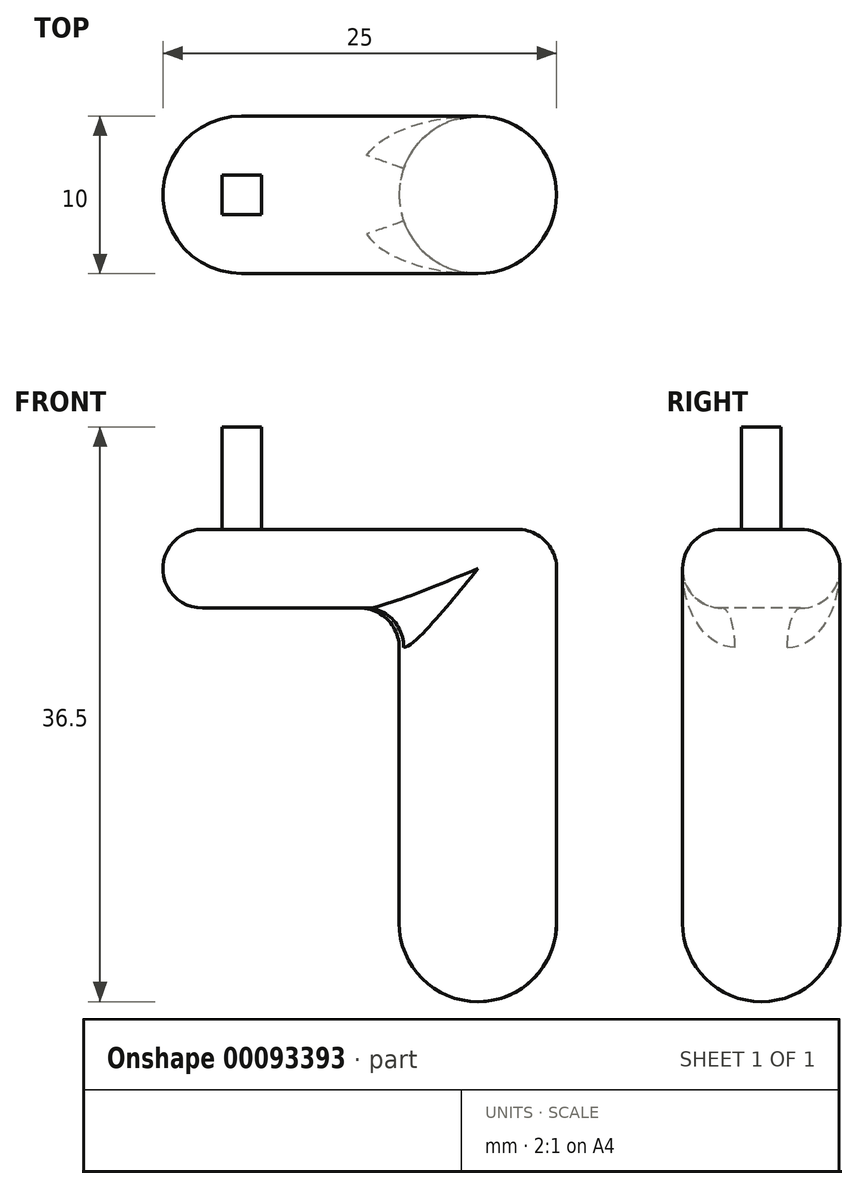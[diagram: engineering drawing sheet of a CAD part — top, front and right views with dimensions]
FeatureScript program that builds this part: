
annotation { "Feature Type Name" : "Feature", "Feature Type Description" : "" }
export const myFeature = defineFeature(function(context is Context, id is Id, definition is map)
    precondition{}
    {
        {
            var Q0;
            Q0=qCreatedBy(makeId("Top.planeOp"),FACE);
            var sketch = newSketch(context, id + "F0", { "sketchPlane" : qUnion([Q0])});
            skLineSegment(sketch, "E0.bottom", {"start": v(0, 0) * mm, "end": v(15, 0) * mm});
            skLineSegment(sketch, "E0.top", {"start": v(0, 10) * mm, "end": v(15, 10) * mm});
            skLineSegment(sketch, "E0.left", {"start": v(0, 0) * mm, "end": v(0, 10) * mm});
            skLineSegment(sketch, "E0.right", {"start": v(15, 0) * mm, "end": v(15, 10) * mm});
            skArc(sketch, "E1", {"start": v(0, 10) * mm, "mid": v(-5, 5) * mm, "end": v(0, 0) * mm});
            skArc(sketch, "E2", {"start": v(15, 0) * mm, "mid": v(20, 5) * mm, "end": v(15, 10) * mm});
            skArc(sketch, "E3", {"start": v(15, 10) * mm, "mid": v(10, 5) * mm, "end": v(15, 0) * mm});
            skLineSegment(sketch, "E4.bottom", {"start": v(1.25, 6.25) * mm, "end": v(-1.25, 6.25) * mm});
            skLineSegment(sketch, "E4.top", {"start": v(1.25, 3.75) * mm, "end": v(-1.25, 3.75) * mm});
            skLineSegment(sketch, "E4.left", {"start": v(1.25, 6.25) * mm, "end": v(1.25, 3.75) * mm});
            skLineSegment(sketch, "E4.right", {"start": v(-1.25, 6.25) * mm, "end": v(-1.25, 3.75) * mm});
            skSolve(sketch);
        }
        {
            var Q0;
            {var subQ5=sQuery(id+"F0.wireOp",EDGE,"E0.bottom");Q0=makeQuery(id+"F0.imprint","IMPRINT",FACE,{"disambiguationData":[TD([[makeQuery(id+"F0.imprint","IMPRINT",EDGE,{"derivedFrom":subQ5}),1.0]])]});}
            var Q1;
            {var subQ4=sQuery(id+"F0.wireOp",EDGE,"E1");Q1=makeQuery(id+"F0.imprint","IMPRINT",FACE,{"disambiguationData":[TD([[makeQuery(id+"F0.imprint","IMPRINT",EDGE,{"derivedFrom":subQ4}),1.0]])]});}
            extrude(context, id + "F1", {"entities" : qUnion([Q0, Q1]), "depth" : 5 * mm});
        }
        {
            var Q0;
            {var subQ5=sQuery(id+"F0.wireOp",EDGE,"E4.right");Q0=makeQuery(id+"F0.imprint","IMPRINT",FACE,{"disambiguationData":[TD([[makeQuery(id+"F0.imprint","IMPRINT",EDGE,{"derivedFrom":subQ5}),1.0]])]});}
            var Q1;
            {var subQ5=sQuery(id+"F0.wireOp",EDGE,"E4.left");Q1=makeQuery(id+"F0.imprint","IMPRINT",FACE,{"disambiguationData":[TD([[makeQuery(id+"F0.imprint","IMPRINT",EDGE,{"derivedFrom":subQ5}),-1.0]])]});}
            extrude(context, id + "F2", {"entities" : qUnion([Q0, Q1]), "operationType" : NewBodyOperationType.ADD, "depth" : 11.5 * mm});
        }
        {
            var Q0;
            Q0=makeQuery(id+"F0.imprint","IMPRINT",FACE,{"disambiguationData":[TD([[makeQuery(id+"F0.imprint","IMPRINT",EDGE,{"derivedFrom":sQuery(id+"F0.wireOp",EDGE,"E0.right")}),1.0]])]});
            var Q1;
            Q1=makeQuery(id+"F0.imprint","IMPRINT",FACE,{"disambiguationData":[TD([[makeQuery(id+"F0.imprint","IMPRINT",EDGE,{"derivedFrom":sQuery(id+"F0.wireOp",EDGE,"E0.right")}),-1.0]])]});
            var Q2;
            Q2=makeQuery(id+"F1.opExtrude","CAP_FACE",FACE,{"disambiguationData":[OSD([sQuery(id+"F0.wireOp",EDGE,"E0.bottom"),sQuery(id+"F0.wireOp",EDGE,"E0.top"),sQuery(id+"F0.wireOp",EDGE,"E1"),sQuery(id+"F0.wireOp",EDGE,"E3"),sQuery(id+"F0.wireOp",EDGE,"E4.bottom"),sQuery(id+"F0.wireOp",EDGE,"E4.top"),sQuery(id+"F0.wireOp",EDGE,"E4.left"),sQuery(id+"F0.wireOp",EDGE,"E4.right")])],"isStart":false});
            extrude(context, id + "F3", {"entities" : qUnion([Q0, Q1]), "operationType" : NewBodyOperationType.ADD, "endBound" : BoundingType.UP_TO_SURFACE, "endBoundEntityFace" : qUnion([Q2]), "depth" : 25 * mm});
        }
        {
            var Q0;
            Q0=makeQuery(id+"F0.imprint","IMPRINT",FACE,{"disambiguationData":[TD([[makeQuery(id+"F0.imprint","IMPRINT",EDGE,{"derivedFrom":sQuery(id+"F0.wireOp",EDGE,"E0.right")}),1.0]])]});
            var Q1;
            Q1=makeQuery(id+"F0.imprint","IMPRINT",FACE,{"disambiguationData":[TD([[makeQuery(id+"F0.imprint","IMPRINT",EDGE,{"derivedFrom":sQuery(id+"F0.wireOp",EDGE,"E0.right")}),-1.0]])]});
            extrude(context, id + "F4", {"entities" : qUnion([Q0, Q1]), "operationType" : NewBodyOperationType.ADD, "oppositeDirection" : true, "depth" : 25 * mm});
        }
        {
            var Q0;
            Q0=makeQuery(id+"F4.opExtrude","CAP_EDGE",EDGE,{"disambiguationData":[OSD([sQuery(id+"F0.wireOp",EDGE,"E2"),sQuery(id+"F0.wireOp",EDGE,"E3")])],"isStart":false});
            fillet(context, id + "F5", {"entities" : qUnion([Q0]), "radius" : 5 * mm, "tangentPropagation" : true, "allowEdgeOverflow" : false});
        }
        {
            var Q0;
            Q0=makeQuery(id+"F1.opExtrude","CAP_EDGE",EDGE,{"disambiguationData":[OSD([sQuery(id+"F0.wireOp",EDGE,"E1")])],"isStart":false});
            fillet(context, id + "F6", {"entities" : qUnion([Q0]), "radius" : 2.5 * mm, "tangentPropagation" : true, "allowEdgeOverflow" : false});
        }
        {
            var Q0;
            {var subQ0=sQuery(id+"F0.wireOp",EDGE,"E3");var subQ1=sQuery(id+"F0.wireOp",EDGE,"E4.right");var subQ2=sQuery(id+"F0.wireOp",EDGE,"E4.left");var subQ3=sQuery(id+"F0.wireOp",EDGE,"E4.top");var subQ4=sQuery(id+"F0.wireOp",EDGE,"E4.bottom");Q0=makeQuery(id+"F3.boolean.opBoolean","MERGE",FACE,{"derivedFrom":[makeQuery(id+"F2.boolean.opBoolean","MERGE",FACE,{"derivedFrom":[makeQuery(id+"F1.opExtrude","CAP_FACE",FACE,{"disambiguationData":[OSD([sQuery(id+"F0.wireOp",EDGE,"E0.bottom"),sQuery(id+"F0.wireOp",EDGE,"E0.top"),sQuery(id+"F0.wireOp",EDGE,"E1"),subQ0,subQ4,subQ3,subQ2,subQ1])],"isStart":true}),makeQuery(id+"F2.opExtrude","CAP_FACE",FACE,{"disambiguationData":[OSD([subQ4,subQ3,subQ2,subQ1])],"isStart":true})]}),makeQuery(id+"F3.opExtrude","CAP_FACE",FACE,{"disambiguationData":[OSD([sQuery(id+"F0.wireOp",EDGE,"E2"),subQ0])],"isStart":true})]});}
            fillet(context, id + "F7", {"entities" : qUnion([Q0]), "radius" : 2.5 * mm, "tangentPropagation" : true, "allowEdgeOverflow" : false});
        }
    });
